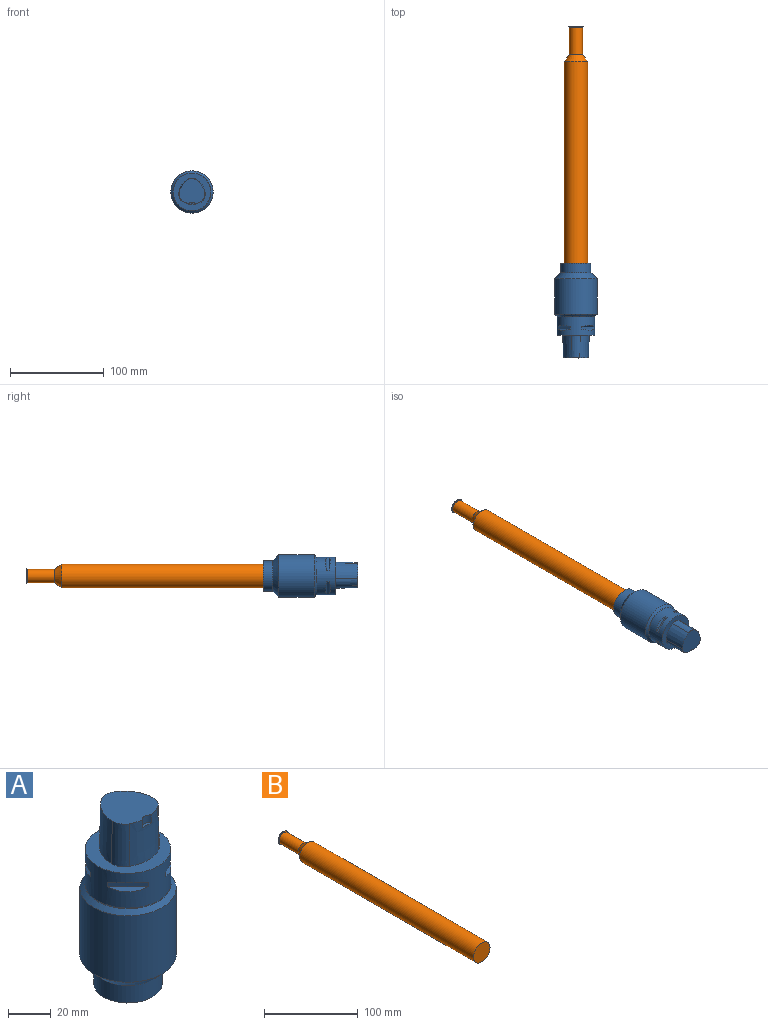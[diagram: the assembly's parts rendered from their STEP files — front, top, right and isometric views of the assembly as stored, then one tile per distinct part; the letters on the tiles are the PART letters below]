
ASSEMBLY  parts=2 mates=1
PART A: 29 faces, bbox 45x45x101 mm
  f0: cylinder r=22.5mm len=45mm, axis (0,0,1), area 5372.1mm2, adj f24,f28
  f1: cone r=20mm half-angle=1.4deg, axis (0,0,-1), area 474.7mm2, adj f2,f6,f7,f8
  f2: cone r=8.5mm half-angle=1.4deg, axis (0,0,-1), area 214.7mm2, adj f1,f3,f7,f8
  f3: cone r=20mm half-angle=1.4deg, axis (0,0,-1), area 477.5mm2, adj f2,f4,f7,f8
  f4: cone r=8.5mm half-angle=1.4deg, axis (0,0,-1), area 214.7mm2, adj f3,f5,f7,f8
  f5: cone r=20mm half-angle=1.4deg, axis (0,0,-1), area 449.4mm2, adj f4,f6,f7,f8,f10,f11
  f6: cone r=8.5mm half-angle=1.4deg, axis (0,0,-1), area 213.4mm2, adj f1,f5,f7,f8
  f7: plane 26.86x26.61mm, normal (0,0,1), area 548.9mm2, adj f1,f2,f3,f4,f5,f6,f11
  f8: plane 40x40mm, normal (0,0,1), area 649.5mm2, adj f1,f2,f3,f4,f5,f6,f9
  f9: cylinder r=20mm len=40mm, axis (0,0,-1), area 2157.4mm2, adj f8,f12,f13,f14,f15,f16,f17,f18
  f10: plane 6.08x1.64mm, normal (0,0,1), area 6.9mm2, adj f5,f11
  f11: cylinder r=4mm len=6.08mm, axis (0,0,-1), area 28.5mm2, adj f5,f7,f10
  f12: plane 13.26x13.26mm, normal (-0.35,-0.35,0.87), area 34.1mm2, adj f9,f13
  f13: plane 13.26x13.26mm, normal (-0.71,-0.71,0), area 46.9mm2, adj f9,f12,f14
  f14: plane 13.26x13.26mm, normal (-0.35,-0.35,-0.87), area 34.1mm2, adj f9,f13
  f15: plane 13.26x13.26mm, normal (-0.35,0.35,0.87), area 34.1mm2, adj f9,f16
  f16: plane 13.26x13.26mm, normal (-0.71,0.71,0), area 46.9mm2, adj f9,f15,f17
  f17: plane 13.26x13.26mm, normal (-0.35,0.35,-0.87), area 34.1mm2, adj f9,f16
  f18: plane 13.26x13.26mm, normal (0.35,0.35,0.87), area 34.1mm2, adj f9,f19
  f19: plane 13.26x13.26mm, normal (0.71,0.71,0), area 46.9mm2, adj f9,f18,f20
  f20: plane 13.26x13.26mm, normal (0.35,0.35,-0.87), area 34.1mm2, adj f9,f19
  f21: plane 13.26x13.26mm, normal (0.35,-0.35,0.87), area 34.1mm2, adj f9,f22
  f22: plane 13.26x13.26mm, normal (0.71,-0.71,0), area 46.9mm2, adj f9,f21,f23
  f23: plane 13.26x13.26mm, normal (0.35,-0.35,-0.87), area 34.1mm2, adj f9,f22
  f24: cone r=22.5mm half-angle=45deg, axis (0,0,-1), area 451.2mm2, adj f0,f25
  f25: torus R=20.4mm, axis (0,0,1), area 39.6mm2, adj f9,f24
  f26: cylinder r=16mm len=32mm, axis (0,0,-1), area 1005.3mm2, adj f27,f28
  f27: plane 32x32mm, normal (0,0,-1), area 804.2mm2, adj f26
  f28: cone r=22.5mm half-angle=45deg, axis (0,0,1), area 1111.8mm2, adj f0,f26
PART B: 7 faces, bbox 25x300x25 mm
  f0: cylinder r=12.5mm len=262.21mm, axis (0,1,0), area 20593.6mm2, adj f1,f2
  f1: plane 25x25mm, normal (0,-1,0), area 490.9mm2, adj f0
  f2: cone r=7mm half-angle=36.2deg, axis (0,-1,0), area 570mm2, adj f0,f5
  f3: cone r=8mm half-angle=60deg, axis (0,1,0), area 54.4mm2, adj f4,f5
  f4: cone r=8mm half-angle=60deg, axis (0,-1,0), area 61.1mm2, adj f3,f6
  f5: cylinder r=7mm len=29.06mm, axis (0,-1,0), area 1278.1mm2, adj f2,f3
  f6: plane 13.74x13.74mm, normal (0,1,0), area 148.2mm2, adj f4
PLACE A rot(axis=(1,0,0),90deg) t=(-69.06,-211.18,-111.2)mm
PLACE B t=(-69.06,118.35,-111.2)mm
MATE cylindrical A.f26 <-> B.f0  axis (0,1,0) through (-69.06,-139.18,-111.2)mm
